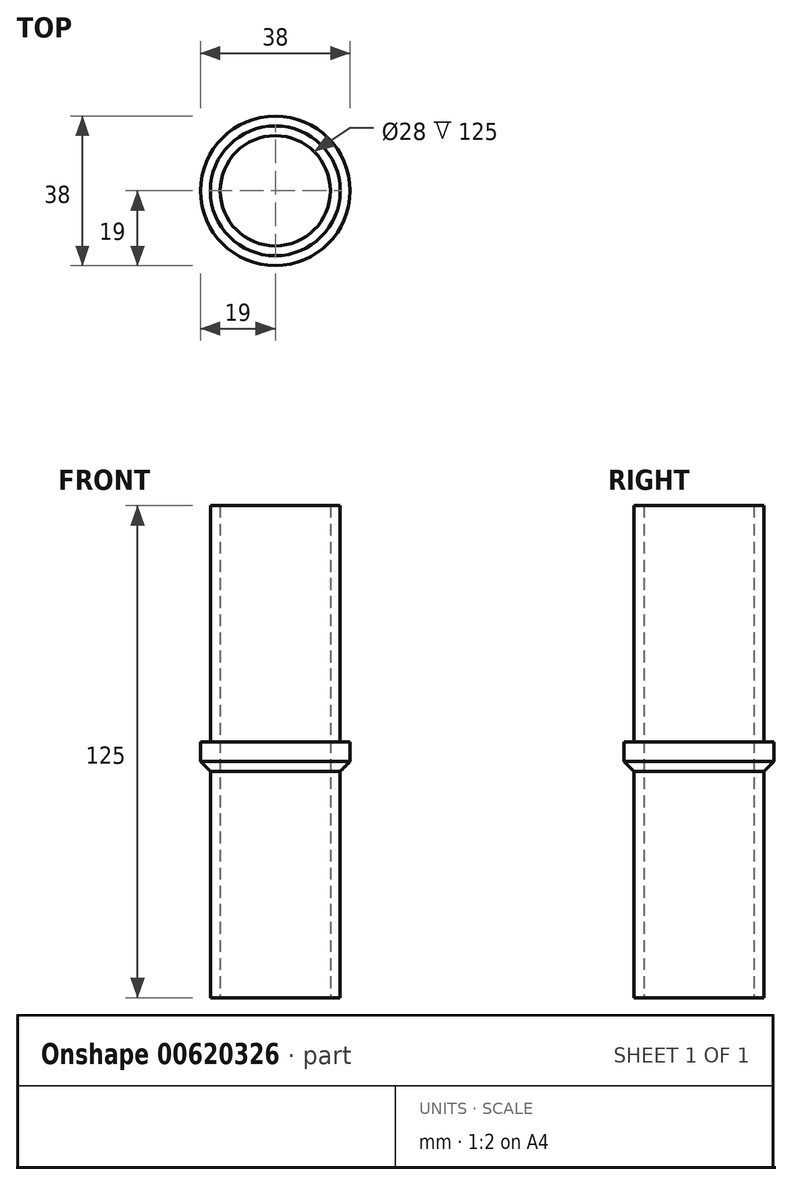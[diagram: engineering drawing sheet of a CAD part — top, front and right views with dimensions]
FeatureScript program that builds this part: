
annotation { "Feature Type Name" : "Feature", "Feature Type Description" : "" }
export const myFeature = defineFeature(function(context is Context, id is Id, definition is map)
    precondition{}
    {
        {
            var Q0;
            Q0=qCreatedBy(makeId("Top.planeOp"),FACE);
            var sketch = newSketch(context, id + "F0", { "sketchPlane" : qUnion([Q0])});
            skCircle(sketch, "E0", {"center": v(0, 0) * mm, "radius": 16.5 * mm});
            skCircle(sketch, "E1.0", {"center": v(0, 0) * mm, "radius": 14 * mm});
            skCircle(sketch, "E2.0", {"center": v(0, 0) * mm, "radius": 19 * mm});
            skSolve(sketch);
        }
        {
            var Q0;
            Q0=makeQuery(id+"F0.imprint","IMPRINT",FACE,{"disambiguationData":[TD([[makeQuery(id+"F0.imprint","IMPRINT",EDGE,{"derivedFrom":sQuery(id+"F0.wireOp",EDGE,"E0")}),1.0]])]});
            extrude(context, id + "F1", {"entities" : qUnion([Q0]), "depth" : 125 * mm, "offsetDistance" : 25 * mm});
        }
        {
            var Q0;
            Q0 = qSketchRegion(id + "F0", true);
            extrude(context, id + "F2", {"entities" : qUnion([Q0]), "operationType" : NewBodyOperationType.ADD, "depth" : 65 * mm, "offsetDistance" : 25 * mm});
        }
        {
            var Q0;
            Q0 = qSketchRegion(id + "F0", true);
            extrude(context, id + "F3", {"entities" : qUnion([Q0]), "operationType" : NewBodyOperationType.REMOVE, "depth" : 60 * mm, "offsetDistance" : 25 * mm});
        }
        {
            var Q0;
            Q0=makeQuery(id+"F3.boolean.opBoolean","COPY",EDGE,{"derivedFrom":makeQuery(id+"F3.opExtrude","CAP_EDGE",EDGE,{"disambiguationData":[OSD([sQuery(id+"F0.wireOp",EDGE,"E0")])],"isStart":false})});
            var Q1;
            Q1=makeQuery(id+"F2.opExtrude","CAP_EDGE",EDGE,{"disambiguationData":[OSD([sQuery(id+"F0.wireOp",EDGE,"E0")])],"isStart":false});
            chamfer(context, id + "F4", {"entities" : qUnion([Q0, Q1]), "width" : 2.5 * mm, "tangentPropagation" : true});
        }
    });
